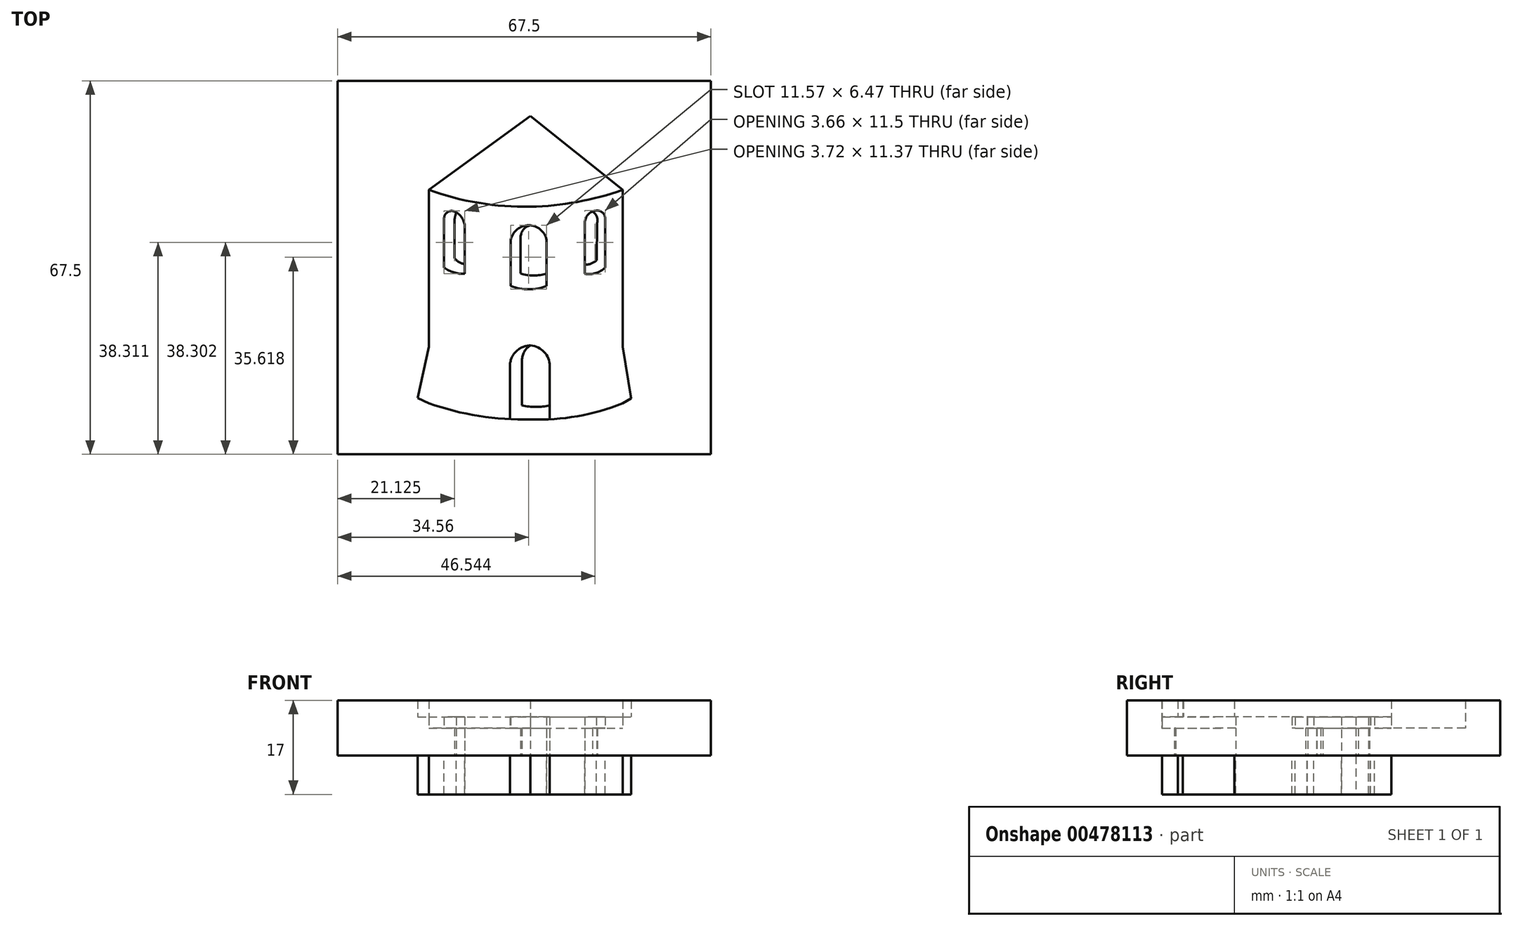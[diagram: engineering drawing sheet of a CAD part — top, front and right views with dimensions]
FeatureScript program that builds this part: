
annotation { "Feature Type Name" : "Feature", "Feature Type Description" : "" }
export const myFeature = defineFeature(function(context is Context, id is Id, definition is map)
    precondition{}
    {
        {
            var Q0;
            Q0=qCreatedBy(makeId("Top.planeOp"),FACE);
            var sketch = newSketch(context, id + "F0", { "sketchPlane" : qUnion([Q0])});
            skLineSegment(sketch, "E0.bottom", {"start": v(-34.9, 33.75) * mm, "end": v(32.6, 33.75) * mm});
            skLineSegment(sketch, "E0.top", {"start": v(-34.9, -33.75) * mm, "end": v(32.6, -33.75) * mm});
            skLineSegment(sketch, "E0.left", {"start": v(-34.9, 33.75) * mm, "end": v(-34.9, -33.75) * mm});
            skLineSegment(sketch, "E0.right", {"start": v(32.6, 33.75) * mm, "end": v(32.6, -33.75) * mm});
            skLineSegment(sketch, "E1", {"start": v(32.6, 33.05) * mm, "end": v(-34.2, 33.05) * mm});
            skLineSegment(sketch, "E2", {"start": v(-34.2, 33.05) * mm, "end": v(-34.2, -33.75) * mm});
            skLineSegment(sketch, "E3", {"start": v(0, 27.43) * mm, "end": v(-18.39, 14.05) * mm});
            skLineSegment(sketch, "E4", {"start": v(0, 27.43) * mm, "end": v(16.65, 14.05) * mm});
            skArc(sketch, "E5", {"start": v(-18.39, 14.05) * mm, "mid": v(-9.33, 11.7) * mm, "end": v(0, 11) * mm});
            skArc(sketch, "E6", {"start": v(0, 11) * mm, "mid": v(8.44, 11.87) * mm, "end": v(16.65, 14.05) * mm});
            skArc(sketch, "E7", {"start": v(-18.39, -24.53) * mm, "mid": v(-9.33, -26.82) * mm, "end": v(0, -27.44) * mm});
            skArc(sketch, "E8", {"start": v(0, -27.44) * mm, "mid": v(8.48, -26.87) * mm, "end": v(16.65, -24.53) * mm});
            skLineSegment(sketch, "E9", {"start": v(-3.73, -27.4) * mm, "end": v(-3.73, -17.8) * mm});
            skLineSegment(sketch, "E10", {"start": v(3.47, -27.43) * mm, "end": v(3.47, -17.8) * mm});
            skArc(sketch, "E11", {"start": v(0, -14.08) * mm, "mid": v(-2.64, -15.17) * mm, "end": v(-3.73, -17.8) * mm});
            skArc(sketch, "E12", {"start": v(3.47, -17.8) * mm, "mid": v(2.47, -15.26) * mm, "end": v(0, -14.08) * mm});
            skLineSegment(sketch, "E13", {"start": v(-3.73, -27.4) * mm, "end": v(-1.54, -24.93) * mm});
            skLineSegment(sketch, "E14", {"start": v(-1.54, -24.93) * mm, "end": v(-1.54, -16.76) * mm});
            skArc(sketch, "E15", {"start": v(0, -14.08) * mm, "mid": v(-1.13, -15.21) * mm, "end": v(-1.54, -16.76) * mm});
            skArc(sketch, "E16", {"start": v(-1.54, -24.93) * mm, "mid": v(0.96, -25.19) * mm, "end": v(3.47, -24.93) * mm});
            skLineSegment(sketch, "E17", {"start": v(-3.57, -3.32) * mm, "end": v(-3.57, 5.02) * mm});
            skLineSegment(sketch, "E18", {"start": v(2.9, -3.32) * mm, "end": v(2.9, 5.02) * mm});
            skArc(sketch, "E19", {"start": v(-3.57, -3.32) * mm, "mid": v(-0.33, -3.92) * mm, "end": v(2.9, -3.32) * mm});
            skArc(sketch, "E20", {"start": v(2.9, 5.02) * mm, "mid": v(-0.33, 7.66) * mm, "end": v(-3.57, 5.02) * mm});
            skLineSegment(sketch, "E21", {"start": v(-3.57, -3.32) * mm, "end": v(-1.79, -1.05) * mm});
            skLineSegment(sketch, "E22", {"start": v(-1.79, -1.05) * mm, "end": v(-1.79, 5.5) * mm});
            skArc(sketch, "E23", {"start": v(0, 7.64) * mm, "mid": v(-1.28, 6.9) * mm, "end": v(-1.79, 5.5) * mm});
            skArc(sketch, "E24", {"start": v(-1.79, -1.05) * mm, "mid": v(0.56, -1.44) * mm, "end": v(2.9, -1.05) * mm});
            skLineSegment(sketch, "E25", {"start": v(-11.9, -1.14) * mm, "end": v(-11.9, 7.36) * mm});
            skLineSegment(sketch, "E26", {"start": v(-15.63, 0) * mm, "end": v(-15.63, 8.9) * mm});
            skArc(sketch, "E27", {"start": v(-15.63, 0) * mm, "mid": v(-13.86, -0.86) * mm, "end": v(-11.9, -1.14) * mm});
            skArc(sketch, "E28", {"start": v(-13.44, 9.95) * mm, "mid": v(-14.86, 10.11) * mm, "end": v(-15.63, 8.9) * mm});
            skArc(sketch, "E29", {"start": v(-11.9, 7.36) * mm, "mid": v(-12.32, 8.87) * mm, "end": v(-13.44, 9.95) * mm});
            skLineSegment(sketch, "E30", {"start": v(-15.63, 0) * mm, "end": v(-13.77, 1.7) * mm});
            skLineSegment(sketch, "E31", {"start": v(-13.77, 1.7) * mm, "end": v(-13.77, 8.1) * mm});
            skArc(sketch, "E32", {"start": v(-13.44, 9.95) * mm, "mid": v(-13.68, 9.04) * mm, "end": v(-13.77, 8.1) * mm});
            skLineSegment(sketch, "E33", {"start": v(-18.39, 14.05) * mm, "end": v(-18.39, -14.33) * mm});
            skLineSegment(sketch, "E34", {"start": v(-18.39, -14.33) * mm, "end": v(-20.4, -23.55) * mm});
            skLineSegment(sketch, "E35", {"start": v(-20.4, -23.55) * mm, "end": v(-18.39, -24.53) * mm});
            skLineSegment(sketch, "E36", {"start": v(16.65, 14.05) * mm, "end": v(16.65, -14.33) * mm});
            skLineSegment(sketch, "E37", {"start": v(16.65, -14.33) * mm, "end": v(18.2, -23.64) * mm});
            skLineSegment(sketch, "E38", {"start": v(18.2, -23.64) * mm, "end": v(16.65, -24.53) * mm});
            skArc(sketch, "E39", {"start": v(-13.77, 1.7) * mm, "mid": v(-12.93, 1) * mm, "end": v(-11.9, 0.6) * mm});
            skLineSegment(sketch, "E40", {"start": v(13.49, 0) * mm, "end": v(13.49, 8.9) * mm});
            skLineSegment(sketch, "E41", {"start": v(9.82, -1.14) * mm, "end": v(9.82, 8.1) * mm});
            skArc(sketch, "E42", {"start": v(9.82, -1.14) * mm, "mid": v(11.79, -1) * mm, "end": v(13.49, 0) * mm});
            skArc(sketch, "E43", {"start": v(11.88, 10.3) * mm, "mid": v(10.42, 9.6) * mm, "end": v(9.82, 8.1) * mm});
            skArc(sketch, "E44", {"start": v(13.49, 8.9) * mm, "mid": v(13, 9.96) * mm, "end": v(11.88, 10.3) * mm});
            skLineSegment(sketch, "E45", {"start": v(13.49, 0) * mm, "end": v(11.94, 1.32) * mm});
            skLineSegment(sketch, "E46", {"start": v(11.94, 1.32) * mm, "end": v(12.04, 8.1) * mm});
            skArc(sketch, "E47", {"start": v(12.04, 8.1) * mm, "mid": v(11.97, 9.26) * mm, "end": v(11.2, 10.14) * mm});
            skArc(sketch, "E48", {"start": v(9.82, 0.51) * mm, "mid": v(10.95, 0.73) * mm, "end": v(11.94, 1.32) * mm});
            skSolve(sketch);
        }
        {
            var Q0;
            {var subQ1=sQuery(id+"F0.wireOp",EDGE,"E0.bottom");Q0=makeQuery(id+"F0.imprint","IMPRINT",FACE,{"disambiguationData":[TD([[makeQuery(id+"F0.imprint","IMPRINT",EDGE,{"derivedFrom":subQ1}),-1.0]])]});}
            extrude(context, id + "F1", {"entities" : qUnion([Q0]), "depth" : 10 * mm});
        }
        {
            var Q0;
            {var subQ11=sQuery(id+"F0.wireOp",EDGE,"E1");Q0=makeQuery(id+"F0.imprint","IMPRINT",FACE,{"disambiguationData":[TD([[makeQuery(id+"F0.imprint","IMPRINT",EDGE,{"derivedFrom":subQ11}),1.0]])]});}
            extrude(context, id + "F2", {"entities" : qUnion([Q0]), "operationType" : NewBodyOperationType.ADD, "depth" : 10 * mm});
        }
        {
            var Q0;
            Q0=makeQuery(id+"F0.imprint","IMPRINT",FACE,{"disambiguationData":[TD([[makeQuery(id+"F0.imprint","IMPRINT",EDGE,{"derivedFrom":sQuery(id+"F0.wireOp",EDGE,"E5")}),-1.0]])]});
            extrude(context, id + "F3", {"entities" : qUnion([Q0]), "operationType" : NewBodyOperationType.ADD, "depth" : 7 * mm});
        }
        {
            var Q0;
            Q0=makeQuery(id+"F0.imprint","IMPRINT",FACE,{"disambiguationData":[TD([[makeQuery(id+"F0.imprint","IMPRINT",EDGE,{"derivedFrom":sQuery(id+"F0.wireOp",EDGE,"E3")}),1.0]])]});
            extrude(context, id + "F4", {"entities" : qUnion([Q0]), "operationType" : NewBodyOperationType.ADD, "depth" : 5 * mm});
        }
        {
            var Q0;
            Q0=makeQuery(id+"F0.imprint","IMPRINT",FACE,{"disambiguationData":[TD([[makeQuery(id+"F0.imprint","IMPRINT",EDGE,{"derivedFrom":sQuery(id+"F0.wireOp",EDGE,"E40")}),1.0]])]});
            var Q1;
            {var subQ0=sQuery(id+"F0.wireOp",EDGE,"E42");Q1=makeQuery(id+"F0.imprint","IMPRINT",FACE,{"disambiguationData":[TD([[makeQuery(id+"F0.imprint","IMPRINT",EDGE,{"derivedFrom":subQ0}),1.0]])]});}
            var Q2;
            {var subQ0=sQuery(id+"F0.wireOp",EDGE,"E19");Q2=makeQuery(id+"F0.imprint","IMPRINT",FACE,{"disambiguationData":[TD([[makeQuery(id+"F0.imprint","IMPRINT",EDGE,{"derivedFrom":subQ0}),1.0]])]});}
            var Q3;
            {var subQ1=sQuery(id+"F0.wireOp",EDGE,"E17");Q3=makeQuery(id+"F0.imprint","IMPRINT",FACE,{"disambiguationData":[TD([[makeQuery(id+"F0.imprint","IMPRINT",EDGE,{"derivedFrom":subQ1}),-1.0]])]});}
            var Q4;
            Q4=makeQuery(id+"F0.imprint","IMPRINT",FACE,{"disambiguationData":[TD([[makeQuery(id+"F0.imprint","IMPRINT",EDGE,{"derivedFrom":sQuery(id+"F0.wireOp",EDGE,"E26")}),-1.0]])]});
            var Q5;
            {var subQ0=sQuery(id+"F0.wireOp",EDGE,"E27");Q5=makeQuery(id+"F0.imprint","IMPRINT",FACE,{"disambiguationData":[TD([[makeQuery(id+"F0.imprint","IMPRINT",EDGE,{"derivedFrom":subQ0}),1.0]])]});}
            var Q6;
            {var subQ0=sQuery(id+"F0.wireOp",EDGE,"E13");Q6=makeQuery(id+"F0.imprint","IMPRINT",FACE,{"disambiguationData":[TD([[makeQuery(id+"F0.imprint","IMPRINT",EDGE,{"derivedFrom":subQ0}),-1.0]])]});}
            var Q7;
            Q7=makeQuery(id+"F0.imprint","IMPRINT",FACE,{"disambiguationData":[TD([[makeQuery(id+"F0.imprint","IMPRINT",EDGE,{"derivedFrom":sQuery(id+"F0.wireOp",EDGE,"E9")}),-1.0]])]});
            extrude(context, id + "F5", {"entities" : qUnion([Q0, Q1, Q2, Q3, Q4, Q5, Q6, Q7]), "operationType" : NewBodyOperationType.ADD, "depth" : 5 * mm});
        }
        {
            var Q0;
            Q0=makeQuery(id+"F0.imprint","IMPRINT",FACE,{"disambiguationData":[TD([[makeQuery(id+"F0.imprint","IMPRINT",EDGE,{"derivedFrom":sQuery(id+"F0.wireOp",EDGE,"E5")}),-1.0]])]});
            extrude(context, id + "F6", {"entities" : qUnion([Q0]), "operationType" : NewBodyOperationType.ADD, "oppositeDirection" : true, "depth" : 7 * mm});
        }
    });
